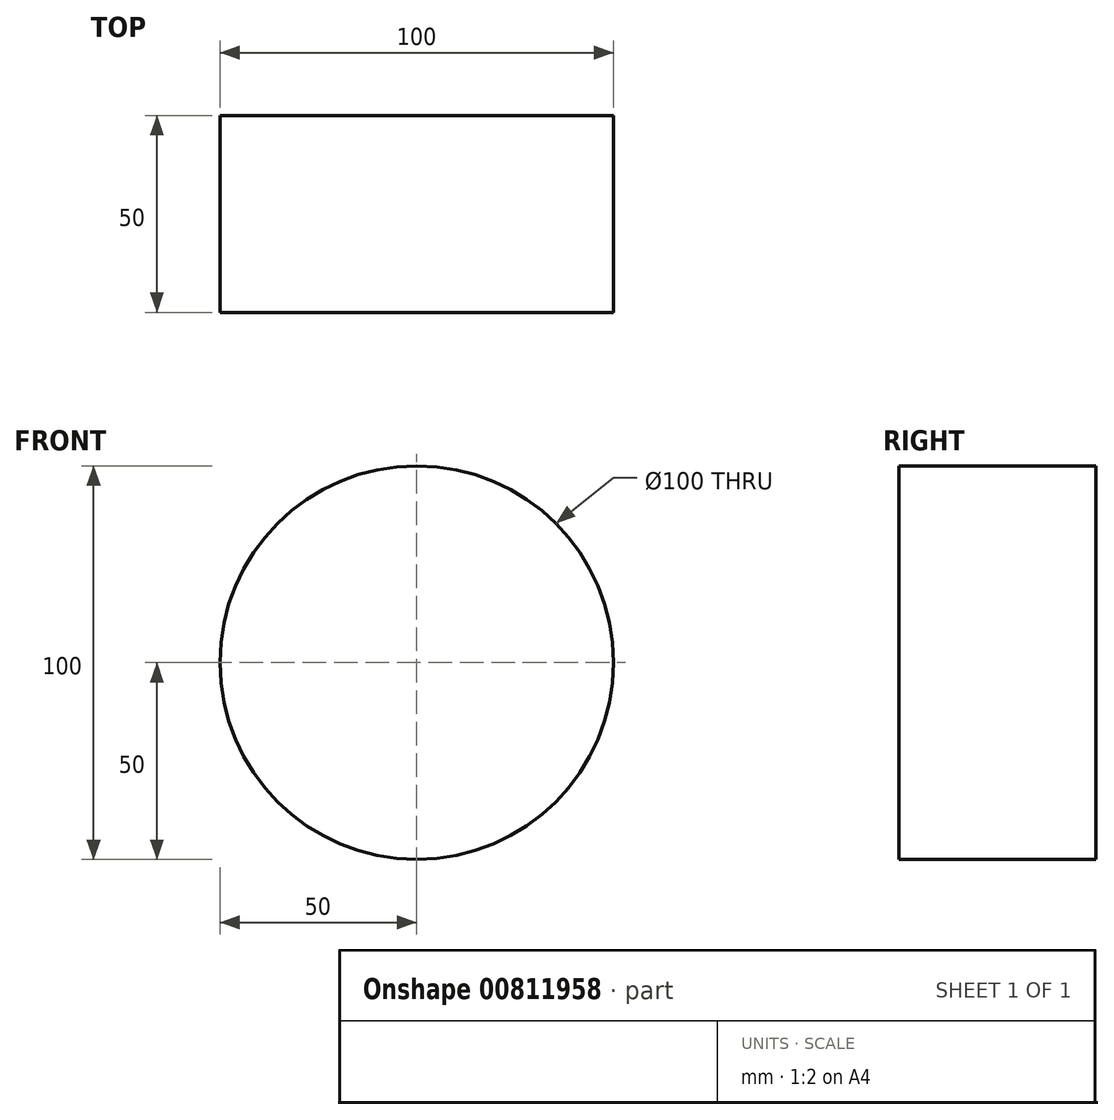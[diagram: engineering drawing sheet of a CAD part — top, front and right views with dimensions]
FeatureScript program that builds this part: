
annotation { "Feature Type Name" : "Feature", "Feature Type Description" : "" }
export const myFeature = defineFeature(function(context is Context, id is Id, definition is map)
    precondition{}
    {
        {
            var Q0;
            Q0=qCreatedBy(makeId("Top.planeOp"),FACE);
            var sketch = newSketch(context, id + "F0", { "sketchPlane" : qUnion([Q0])});
            skLineSegment(sketch, "E0.bottom", {"start": v(25, -25) * mm, "end": v(-25, -25) * mm});
            skLineSegment(sketch, "E0.top", {"start": v(25, 25) * mm, "end": v(-25, 25) * mm});
            skLineSegment(sketch, "E0.left", {"start": v(25, -25) * mm, "end": v(25, 25) * mm});
            skLineSegment(sketch, "E0.right", {"start": v(-25, -25) * mm, "end": v(-25, 25) * mm});
            skPoint(sketch, "E0.middle", {"position": v(0, 0) * mm});
            skSolve(sketch);
        }
        {
            var Q0;
            Q0=sQuery(id+"F0.wireOp",EDGE,"E0.left");
            var Q1;
            Q1=sQuery(id+"F0.wireOp",EDGE,"E0.right");
            revolve(context, id + "F1", {"bodyType" : ToolBodyType.SURFACE, "surfaceOperationType" : NewSurfaceOperationType.NEW, "surfaceEntities" : qUnion([Q0]), "axis" : qUnion([Q1]), "revolveType" : RevolveType.FULL});
        }
    });
